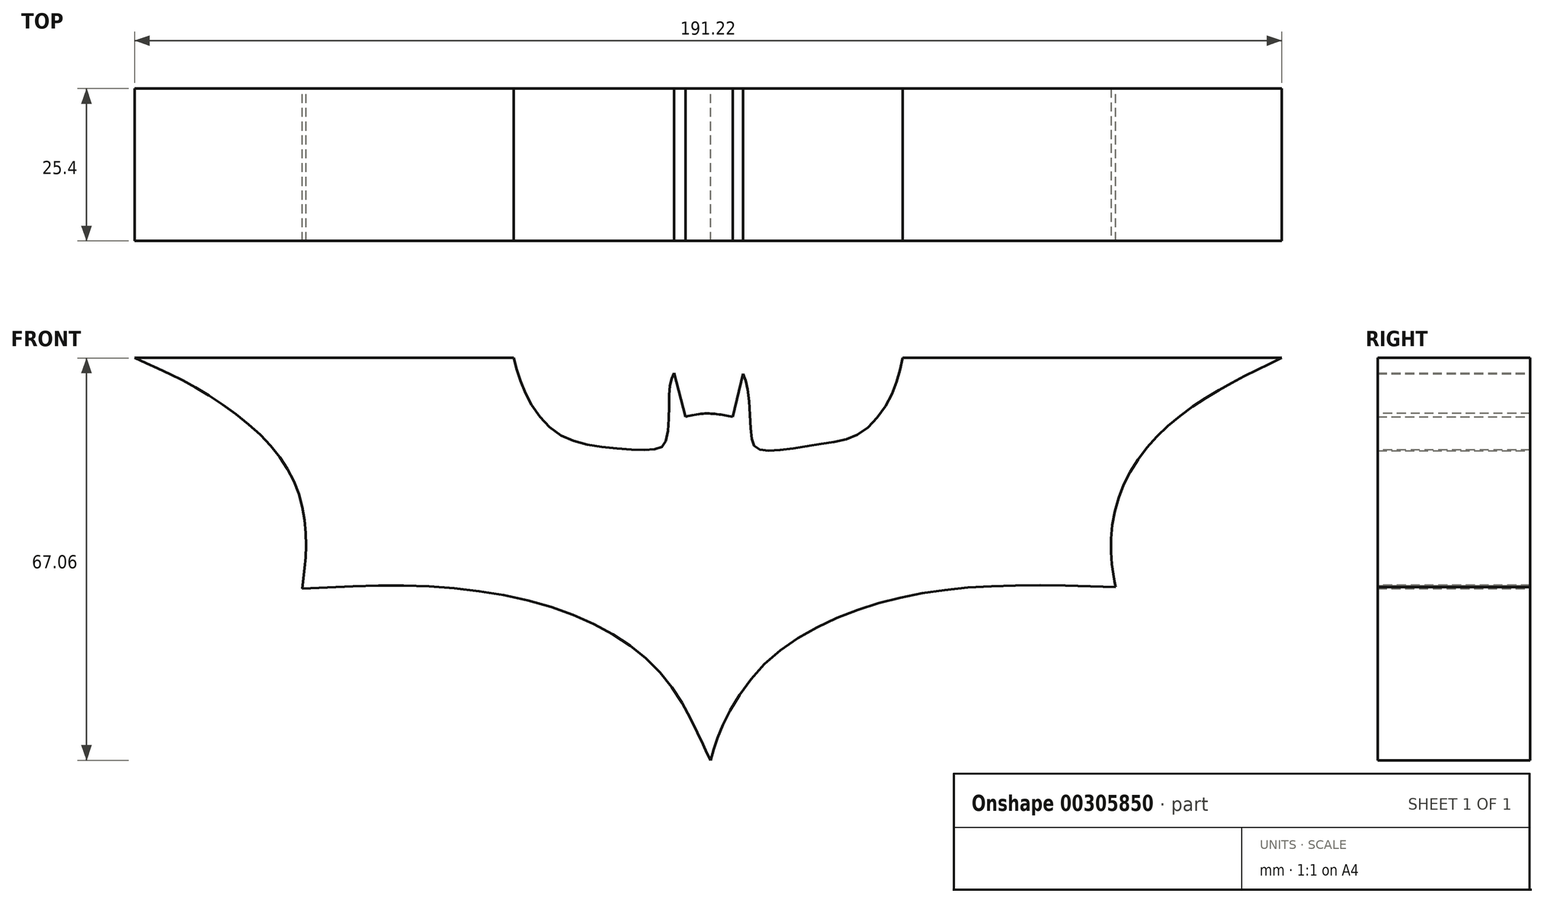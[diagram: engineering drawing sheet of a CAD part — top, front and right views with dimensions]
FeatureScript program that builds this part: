
annotation { "Feature Type Name" : "Feature", "Feature Type Description" : "" }
export const myFeature = defineFeature(function(context is Context, id is Id, definition is map)
    precondition{}
    {
        {
            var Q0;
            Q0=qCreatedBy(makeId("Front.planeOp"),FACE);
            var sketch = newSketch(context, id + "F0", { "sketchPlane" : qUnion([Q0])});
            skLineSegment(sketch, "E0", {"start": v(-93.6, 50.82) * mm, "end": v(-30.4, 50.82) * mm});
            skLineSegment(sketch, "E1", {"start": v(34.42, 50.82) * mm, "end": v(97.62, 50.82) * mm});
            skLineSegment(sketch, "E2", {"start": v(7.85, 48.2) * mm, "end": v(6.04, 40.76) * mm});
            skLineSegment(sketch, "E3", {"start": v(-3.67, 48.33) * mm, "end": v(-1.76, 41.03) * mm});
            skFitSpline(sketch, "E4", {"points": [v(-1.76, 41.03) * mm, v(1.2, 41.54) * mm, v(3.67, 41.44) * mm, v(6.1, 41.03) * mm], "startDerivative": vector(8.53, 1.83) * mm, "endDerivative": vector(7.57, -1.4) * mm});
            skFitSpline(sketch, "E5", {"points": [v(-30.4, 50.82) * mm, v(-28.24, 44.54) * mm, v(-22.89, 38.13) * mm, v(-14.37, 35.87) * mm, v(-6.98, 35.57) * mm, v(-5.17, 36.63) * mm, v(-4.5, 42.13) * mm, v(-4.27, 46.65) * mm, v(-3.67, 48.33) * mm], "startDerivative": vector(11.8, -44.29) * mm, "endDerivative": vector(9.45, 20.48) * mm});
            skFitSpline(sketch, "E6", {"points": [v(34.42, 50.82) * mm, v(32.45, 44.4) * mm, v(27.48, 38.36) * mm, v(21.22, 36.55) * mm, v(13.38, 35.42) * mm, v(9.98, 35.87) * mm, v(9.15, 38.28) * mm, v(8.63, 45.45) * mm, v(7.85, 48.2) * mm], "startDerivative": vector(-9.9, -45.75) * mm, "endDerivative": vector(-9.63, 24.95) * mm});
            skFitSpline(sketch, "E7", {"points": [v(-93.6, 50.82) * mm, v(-84.31, 46.38) * mm, v(-72.48, 37.86) * mm, v(-66.3, 28.36) * mm, v(-65.04, 18.85) * mm, v(-65.66, 12.4) * mm], "startDerivative": vector(44.56, -19.41) * mm, "endDerivative": vector(-5.4, -38.41) * mm});
            skFitSpline(sketch, "E8", {"points": [v(97.62, 50.82) * mm, v(88.92, 46.47) * mm, v(79.1, 39.88) * mm, v(72.12, 31.38) * mm, v(69.27, 22.06) * mm, v(69.52, 14.83) * mm, v(69.97, 12.62) * mm], "startDerivative": vector(-47.04, -22.34) * mm, "endDerivative": vector(5.12, -21.6) * mm});
            skFitSpline(sketch, "E9", {"points": [v(69.97, 12.62) * mm, v(46.34, 12.62) * mm, v(27.2, 8.9) * mm, v(11.64, 0) * mm, v(4.33, -10.73) * mm, v(2.42, -16.24) * mm], "startDerivative": vector(-97.35, 3.18) * mm, "endDerivative": vector(-11.85, -40.95) * mm});
            skFitSpline(sketch, "E10", {"points": [v(-65.66, 12.4) * mm, v(-39.83, 12.4) * mm, v(-17.33, 6.62) * mm, v(-4.4, -3.55) * mm, v(0.98, -13.24) * mm, v(2.42, -16.24) * mm], "startDerivative": vector(97.64, 4.68) * mm, "endDerivative": vector(13.12, -26.6) * mm});
            skSolve(sketch);
        }
        {
            var Q0;
            Q0 = qSketchRegion(id + "F0", true);
            extrude(context, id + "F1", {"entities" : qUnion([Q0]), "depth" : 25.4 * mm});
        }
    });
